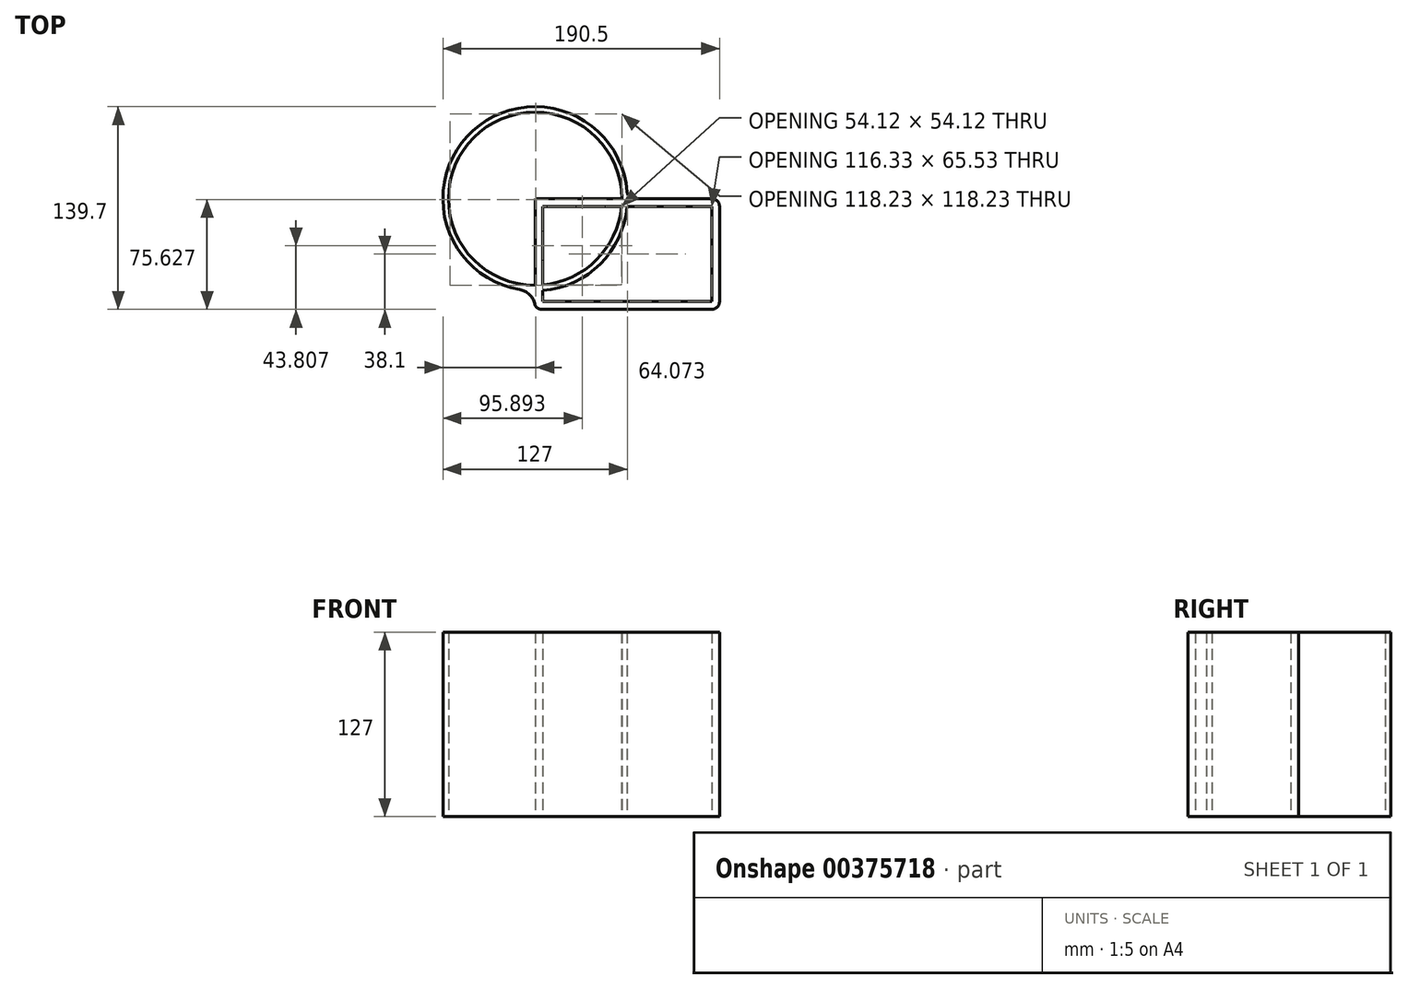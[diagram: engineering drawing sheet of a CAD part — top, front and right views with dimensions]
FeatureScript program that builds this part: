
annotation { "Feature Type Name" : "Feature", "Feature Type Description" : "" }
export const myFeature = defineFeature(function(context is Context, id is Id, definition is map)
    precondition{}
    {
        {
            var Q0;
            Q0=qCreatedBy(makeId("Top.planeOp"),FACE);
            var sketch = newSketch(context, id + "F0", { "sketchPlane" : qUnion([Q0])});
            skCircle(sketch, "E0", {"center": v(0, 0) * mm, "radius": 63.5 * mm});
            skCircle(sketch, "E1", {"center": v(0, 0) * mm, "radius": 59.7 * mm});
            skSolve(sketch);
        }
        {
            var Q0;
            Q0 = qSketchRegion(id + "F0", true);
            extrude(context, id + "F1", {"entities" : qUnion([Q0]), "depth" : 127 * mm});
        }
        {
            var Q0;
            Q0=qCreatedBy(makeId("Top.planeOp"),FACE);
            var sketch = newSketch(context, id + "F2", { "sketchPlane" : qUnion([Q0])});
            skLineSegment(sketch, "E2.bottom", {"start": v(0, 0) * mm, "end": v(127, 0) * mm});
            skLineSegment(sketch, "E2.top", {"start": v(0, -76.2) * mm, "end": v(127, -76.2) * mm});
            skLineSegment(sketch, "E2.left", {"start": v(0, 0) * mm, "end": v(0, -76.2) * mm});
            skLineSegment(sketch, "E2.right", {"start": v(127, 0) * mm, "end": v(127, -76.2) * mm});
            skLineSegment(sketch, "E3.0", {"start": v(5.33, -5.33) * mm, "end": v(5.33, -70.87) * mm});
            skLineSegment(sketch, "E3.1", {"start": v(5.33, -5.33) * mm, "end": v(121.67, -5.33) * mm});
            skLineSegment(sketch, "E3.2", {"start": v(121.67, -5.33) * mm, "end": v(121.67, -70.87) * mm});
            skLineSegment(sketch, "E3.3", {"start": v(5.33, -70.87) * mm, "end": v(121.67, -70.87) * mm});
            skSolve(sketch);
        }
        {
            var Q0;
            Q0=makeQuery(id+"F2.imprint","IMPRINT",FACE,{"disambiguationData":[TD([[makeQuery(id+"F2.imprint","IMPRINT",EDGE,{"derivedFrom":sQuery(id+"F2.wireOp",EDGE,"E2.bottom")}),-1.0]])]});
            extrude(context, id + "F3", {"entities" : qUnion([Q0]), "operationType" : NewBodyOperationType.ADD, "depth" : 127 * mm});
        }
        {
            var Q0;
            Q0=makeQuery(id+"F3.boolean.opBoolean","INTERSECT",EDGE,{"derivedFrom":[makeQuery(id+"F1.opExtrude","SWEPT_FACE",FACE,{"disambiguationData":[OSD([sQuery(id+"F0.wireOp",EDGE,"E0")])]}),makeQuery(id+"F3.opExtrude","SWEPT_FACE",FACE,{"disambiguationData":[OSD([sQuery(id+"F2.wireOp",EDGE,"E2.left")])]})]});
            fillet(context, id + "F4", {"entities" : qUnion([Q0]), "radius" : 12.7 * mm, "tangentPropagation" : true, "allowEdgeOverflow" : false});
        }
        {
            var Q0;
            Q0=makeQuery(id+"F3.boolean.opBoolean","INTERSECT",EDGE,{"derivedFrom":[makeQuery(id+"F1.opExtrude","SWEPT_FACE",FACE,{"disambiguationData":[OSD([sQuery(id+"F0.wireOp",EDGE,"E0")])]}),makeQuery(id+"F3.opExtrude","SWEPT_FACE",FACE,{"disambiguationData":[OSD([sQuery(id+"F2.wireOp",EDGE,"E2.bottom")])]})]});
            fillet(context, id + "F5", {"entities" : qUnion([Q0]), "radius" : 5.08 * mm, "tangentPropagation" : true, "allowEdgeOverflow" : false});
        }
        {
            var Q0;
            Q0=makeQuery(id+"F3.opExtrude","SWEPT_EDGE",EDGE,{"disambiguationData":[OSD([sQuery(id+"F2.wireOp",EDGE,"E2.bottom"),sQuery(id+"F2.wireOp",EDGE,"E2.right")])]});
            fillet(context, id + "F6", {"entities" : qUnion([Q0]), "radius" : 5.08 * mm, "tangentPropagation" : true, "allowEdgeOverflow" : false});
        }
        {
            var Q0;
            Q0=makeQuery(id+"F3.opExtrude","SWEPT_EDGE",EDGE,{"disambiguationData":[OSD([sQuery(id+"F2.wireOp",EDGE,"E2.top"),sQuery(id+"F2.wireOp",EDGE,"E2.right")])]});
            fillet(context, id + "F7", {"entities" : qUnion([Q0]), "radius" : 5.08 * mm, "tangentPropagation" : true, "allowEdgeOverflow" : false});
        }
        {
            var Q0;
            Q0=makeQuery(id+"F3.opExtrude","SWEPT_EDGE",EDGE,{"disambiguationData":[OSD([sQuery(id+"F2.wireOp",EDGE,"E2.top"),sQuery(id+"F2.wireOp",EDGE,"E2.left")])]});
            fillet(context, id + "F8", {"entities" : qUnion([Q0]), "radius" : 5.08 * mm, "tangentPropagation" : true, "allowEdgeOverflow" : false});
        }
    });
